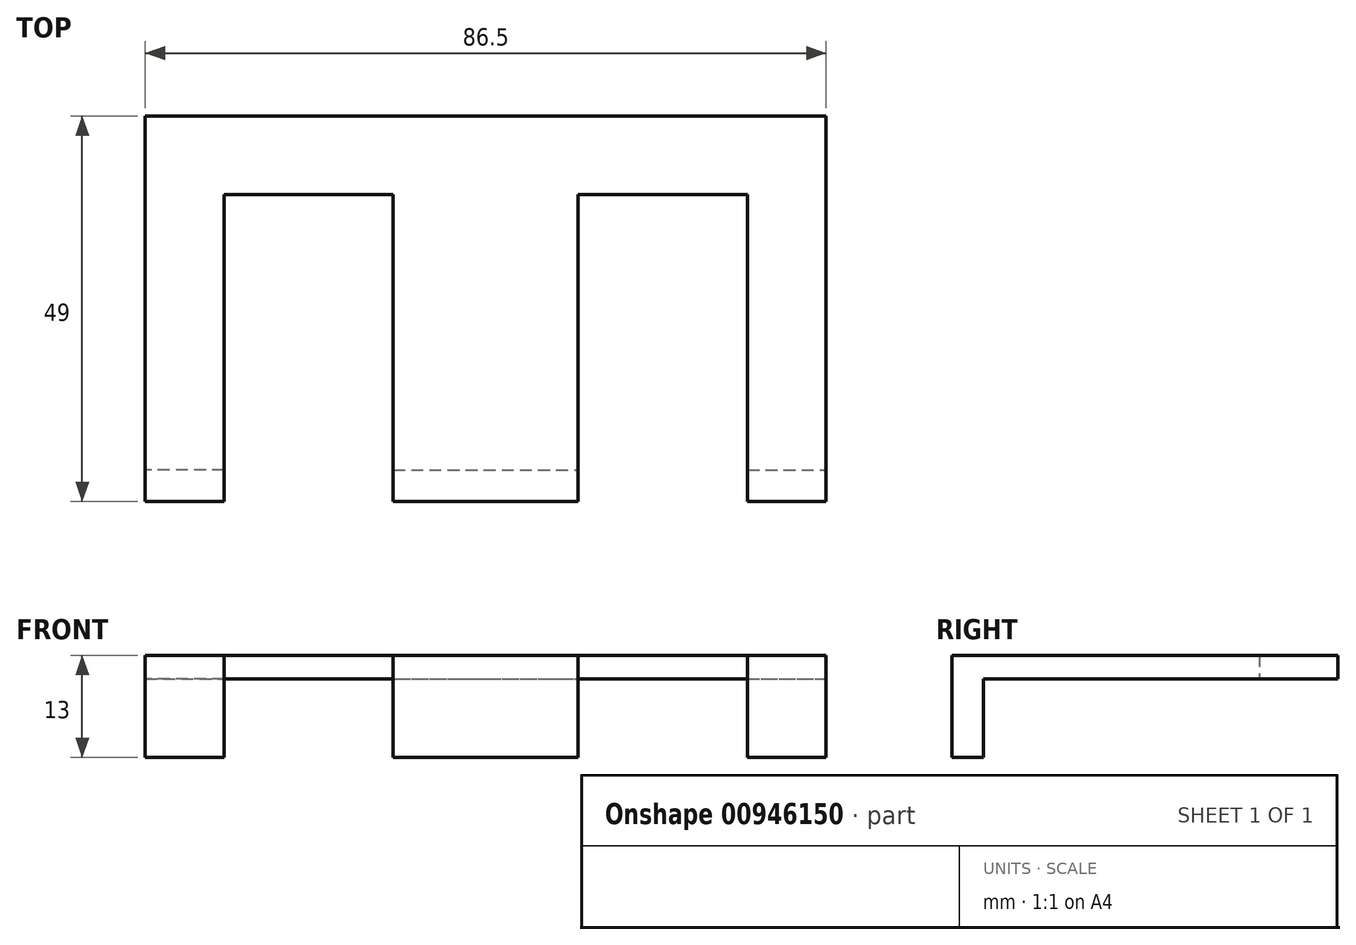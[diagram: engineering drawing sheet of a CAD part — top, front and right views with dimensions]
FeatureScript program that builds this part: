
annotation { "Feature Type Name" : "Feature", "Feature Type Description" : "" }
export const myFeature = defineFeature(function(context is Context, id is Id, definition is map)
    precondition{}
    {
        {
            var Q0;
            Q0=qCreatedBy(makeId("Top.planeOp"),FACE);
            var sketch = newSketch(context, id + "F0", { "sketchPlane" : qUnion([Q0])});
            skLineSegment(sketch, "E0.bottom", {"start": v(-10.75, 0) * mm, "end": v(10.75, 0) * mm});
            skLineSegment(sketch, "E0.top", {"start": v(-10.75, -35) * mm, "end": v(10.75, -35) * mm});
            skLineSegment(sketch, "E0.left", {"start": v(-10.75, 0) * mm, "end": v(-10.75, -35) * mm});
            skLineSegment(sketch, "E0.right", {"start": v(10.75, 0) * mm, "end": v(10.75, -35) * mm});
            skPoint(sketch, "E1", {"position": v(0, 0) * mm});
            skLineSegment(sketch, "E2.bottom", {"start": v(34.25, 0) * mm, "end": v(55.75, 0) * mm});
            skLineSegment(sketch, "E2.top", {"start": v(34.25, -35) * mm, "end": v(55.75, -35) * mm});
            skLineSegment(sketch, "E2.left", {"start": v(34.25, 0) * mm, "end": v(34.25, -35) * mm});
            skLineSegment(sketch, "E2.right", {"start": v(55.75, 0) * mm, "end": v(55.75, -35) * mm});
            skPoint(sketch, "E3", {"position": v(45, 0) * mm});
            skLineSegment(sketch, "E4.bottom", {"start": v(-20, 13) * mm, "end": v(20, 13) * mm, "construction": true});
            skLineSegment(sketch, "E4.top", {"start": v(-20, -79) * mm, "end": v(20, -79) * mm, "construction": true});
            skLineSegment(sketch, "E4.left", {"start": v(-20, 13) * mm, "end": v(-20, -79) * mm, "construction": true});
            skLineSegment(sketch, "E4.right", {"start": v(20, 13) * mm, "end": v(20, -79) * mm, "construction": true});
            skPoint(sketch, "E5", {"position": v(0, 13) * mm});
            skLineSegment(sketch, "E6.bottom", {"start": v(25, 13) * mm, "end": v(65, 13) * mm, "construction": true});
            skLineSegment(sketch, "E6.top", {"start": v(25, -79) * mm, "end": v(65, -79) * mm, "construction": true});
            skLineSegment(sketch, "E6.left", {"start": v(25, 13) * mm, "end": v(25, -79) * mm, "construction": true});
            skLineSegment(sketch, "E6.right", {"start": v(65, 13) * mm, "end": v(65, -79) * mm, "construction": true});
            skPoint(sketch, "E7", {"position": v(45, 13) * mm});
            skLineSegment(sketch, "E8", {"start": v(-20.75, -39) * mm, "end": v(65.75, -39) * mm});
            skLineSegment(sketch, "E9", {"start": v(-20.75, -39) * mm, "end": v(-20.75, 10) * mm});
            skLineSegment(sketch, "E10", {"start": v(-20.75, 10) * mm, "end": v(65.75, 10) * mm});
            skLineSegment(sketch, "E11", {"start": v(65.75, 10) * mm, "end": v(65.75, -39) * mm});
            skLineSegment(sketch, "E12", {"start": v(-10.75, -35) * mm, "end": v(-20.75, -35) * mm});
            skLineSegment(sketch, "E13", {"start": v(10.75, -35) * mm, "end": v(34.25, -35) * mm});
            skLineSegment(sketch, "E14", {"start": v(55.75, -35) * mm, "end": v(65.75, -35) * mm});
            skLineSegment(sketch, "E15", {"start": v(-10.75, -35) * mm, "end": v(-10.75, -39) * mm});
            skLineSegment(sketch, "E16", {"start": v(10.75, -35) * mm, "end": v(10.75, -39) * mm});
            skLineSegment(sketch, "E17", {"start": v(34.25, -35) * mm, "end": v(34.25, -39) * mm});
            skLineSegment(sketch, "E18", {"start": v(55.75, -35) * mm, "end": v(55.75, -39) * mm});
            skSolve(sketch);
        }
        {
            var Q0;
            Q0=makeQuery(id+"F0.imprint","IMPRINT",FACE,{"disambiguationData":[TD([[makeQuery(id+"F0.imprint","IMPRINT",EDGE,{"derivedFrom":sQuery(id+"F0.wireOp",EDGE,"E0.bottom")}),1.0]])]});
            var Q1;
            {var subQ4=sQuery(id+"F0.wireOp",EDGE,"E12");Q1=makeQuery(id+"F0.imprint","IMPRINT",FACE,{"disambiguationData":[TD([[makeQuery(id+"F0.imprint","IMPRINT",EDGE,{"derivedFrom":subQ4}),1.0]])]});}
            var Q2;
            Q2=makeQuery(id+"F0.imprint","IMPRINT",FACE,{"disambiguationData":[TD([[makeQuery(id+"F0.imprint","IMPRINT",EDGE,{"derivedFrom":sQuery(id+"F0.wireOp",EDGE,"E13")}),-1.0]])]});
            var Q3;
            {var subQ4=sQuery(id+"F0.wireOp",EDGE,"E14");Q3=makeQuery(id+"F0.imprint","IMPRINT",FACE,{"disambiguationData":[TD([[makeQuery(id+"F0.imprint","IMPRINT",EDGE,{"derivedFrom":subQ4}),-1.0]])]});}
            extrude(context, id + "F1", {"entities" : qUnion([Q0, Q1, Q2, Q3]), "depth" : 3 * mm, "offsetDistance" : 25 * mm});
        }
        {
            var Q0;
            {var subQ4=sQuery(id+"F0.wireOp",EDGE,"E12");Q0=makeQuery(id+"F0.imprint","IMPRINT",FACE,{"disambiguationData":[TD([[makeQuery(id+"F0.imprint","IMPRINT",EDGE,{"derivedFrom":subQ4}),1.0]])]});}
            var Q1;
            Q1=makeQuery(id+"F0.imprint","IMPRINT",FACE,{"disambiguationData":[TD([[makeQuery(id+"F0.imprint","IMPRINT",EDGE,{"derivedFrom":sQuery(id+"F0.wireOp",EDGE,"E13")}),-1.0]])]});
            var Q2;
            {var subQ4=sQuery(id+"F0.wireOp",EDGE,"E14");Q2=makeQuery(id+"F0.imprint","IMPRINT",FACE,{"disambiguationData":[TD([[makeQuery(id+"F0.imprint","IMPRINT",EDGE,{"derivedFrom":subQ4}),-1.0]])]});}
            extrude(context, id + "F2", {"entities" : qUnion([Q0, Q1, Q2]), "operationType" : NewBodyOperationType.ADD, "oppositeDirection" : true, "depth" : 10 * mm, "offsetDistance" : 25 * mm});
        }
    });
